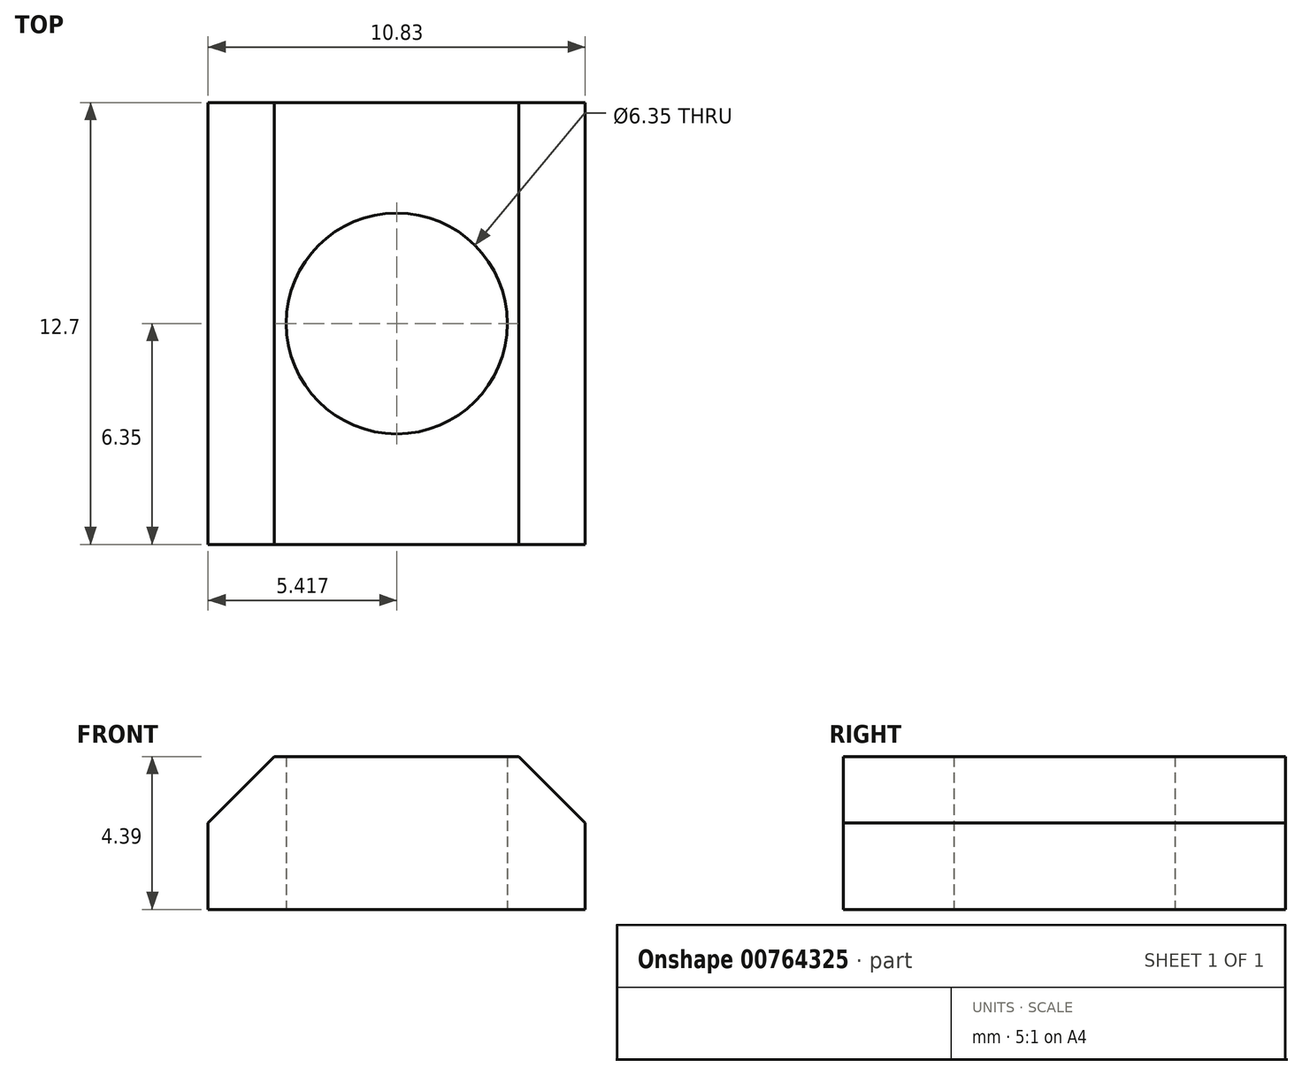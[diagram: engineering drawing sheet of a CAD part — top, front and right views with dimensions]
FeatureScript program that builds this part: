
annotation { "Feature Type Name" : "Feature", "Feature Type Description" : "" }
export const myFeature = defineFeature(function(context is Context, id is Id, definition is map)
    precondition{}
    {
        {
            var Q0;
            Q0=qCreatedBy(makeId("Front.planeOp"),FACE);
            var sketch = newSketch(context, id + "F0", { "sketchPlane" : qUnion([Q0])});
            skLineSegment(sketch, "E0", {"start": v(0, 0) * mm, "end": v(10.83, 0) * mm});
            skLineSegment(sketch, "E1", {"start": v(10.83, 0) * mm, "end": v(10.83, 4.4) * mm});
            skLineSegment(sketch, "E2", {"start": v(10.83, 4.4) * mm, "end": v(0, 4.4) * mm});
            skLineSegment(sketch, "E3", {"start": v(0, 4.4) * mm, "end": v(0, 0) * mm});
            skSolve(sketch);
        }
        {
            var Q0;
            Q0=qSketchRegion(id+"F0",true);
            extrude(context, id + "F1", {"entities" : qUnion([Q0]), "depth" : 12.7 * mm});
        }
        {
            var Q0;
            Q0=makeQuery(id+"F1.opExtrude","SWEPT_EDGE",EDGE,{"disambiguationData":[OSD([sQuery(id+"F0.wireOp",EDGE,"E1"),sQuery(id+"F0.wireOp",EDGE,"E2")])]});
            var Q1;
            Q1=makeQuery(id+"F1.opExtrude","SWEPT_EDGE",EDGE,{"disambiguationData":[OSD([sQuery(id+"F0.wireOp",EDGE,"E2"),sQuery(id+"F0.wireOp",EDGE,"E3")])]});
            chamfer(context, id + "F2", {"entities" : qUnion([Q0, Q1]), "width" : 1.9 * mm, "tangentPropagation" : true});
        }
        {
            var Q0;
            Q0=makeQuery(id+"F1.opExtrude","SWEPT_FACE",FACE,{"disambiguationData":[OSD([sQuery(id+"F0.wireOp",EDGE,"E0")])]});
            var sketch = newSketch(context, id + "F3", { "sketchPlane" : qUnion([Q0])});
            skCircle(sketch, "E4", {"center": v(5.42, 6.35) * mm, "radius": 3.18 * mm});
            skPoint(sketch, "E4.centerSnap0", {"position": v(0, 6.35) * mm});
            skPoint(sketch, "E4.centerSnap1", {"position": v(5.42, 0) * mm});
            skSolve(sketch);
        }
        {
            var Q0;
            Q0=qSketchRegion(id+"F3",true);
            extrude(context, id + "F4", {"entities" : qUnion([Q0]), "operationType" : NewBodyOperationType.REMOVE, "oppositeDirection" : true, "depth" : 25.4 * mm});
        }
    });
